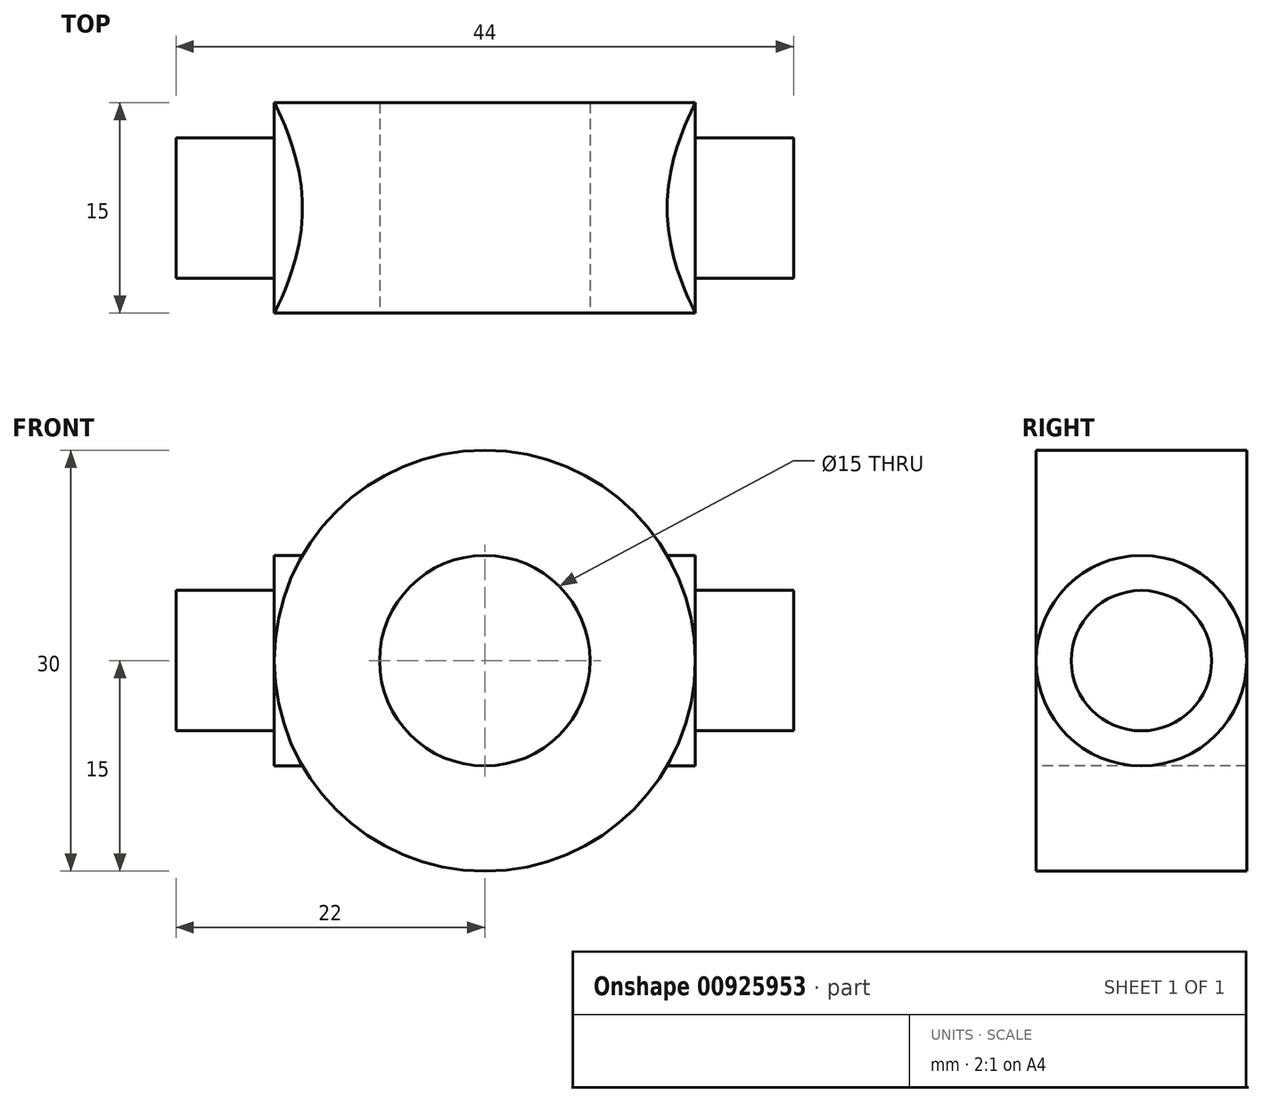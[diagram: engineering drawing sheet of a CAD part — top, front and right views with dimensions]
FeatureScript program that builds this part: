
annotation { "Feature Type Name" : "Feature", "Feature Type Description" : "" }
export const myFeature = defineFeature(function(context is Context, id is Id, definition is map)
    precondition{}
    {
        {
            var Q0;
            Q0=qCreatedBy(makeId("Front.planeOp"),FACE);
            var sketch = newSketch(context, id + "F0", { "sketchPlane" : qUnion([Q0])});
            skCircle(sketch, "E0", {"center": v(0, 0) * mm, "radius": 15 * mm});
            skSolve(sketch);
        }
        {
            var Q0;
            Q0=makeQuery(id+"F0.imprint","IMPRINT",FACE,{"disambiguationData":[TD([[makeQuery(id+"F0.imprint","IMPRINT",EDGE,{"derivedFrom":sQuery(id+"F0.wireOp",EDGE,"E0")}),1.0]])]});
            extrude(context, id + "F1", {"entities" : qUnion([Q0]), "endBound" : BoundingType.SYMMETRIC, "depth" : 15 * mm, "offsetDistance" : 25 * mm});
        }
        {
            var Q0;
            Q0=qCreatedBy(makeId("Right.planeOp"),FACE);
            var sketch = newSketch(context, id + "F2", { "sketchPlane" : qUnion([Q0])});
            skCircle(sketch, "E1", {"center": v(0, 0) * mm, "radius": 7.5 * mm});
            skSolve(sketch);
        }
        {
            var Q0;
            Q0 = qSketchRegion(id + "F2", true);
            extrude(context, id + "F3", {"entities" : qUnion([Q0]), "operationType" : NewBodyOperationType.ADD, "endBound" : BoundingType.SYMMETRIC, "depth" : 30 * mm, "offsetDistance" : 25 * mm});
        }
        {
            var Q0;
            Q0=qCreatedBy(makeId("Right.planeOp"),FACE);
            var sketch = newSketch(context, id + "F4", { "sketchPlane" : qUnion([Q0])});
            skCircle(sketch, "E2", {"center": v(0, 0) * mm, "radius": 5 * mm});
            skSolve(sketch);
        }
        {
            var Q0;
            Q0 = qSketchRegion(id + "F4", true);
            extrude(context, id + "F5", {"entities" : qUnion([Q0]), "operationType" : NewBodyOperationType.ADD, "endBound" : BoundingType.SYMMETRIC, "depth" : 44 * mm, "offsetDistance" : 25 * mm});
        }
        {
            var Q0;
            Q0=makeQuery(id+"F1.opExtrude","CAP_FACE",FACE,{"disambiguationData":[OSD([sQuery(id+"F0.wireOp",EDGE,"E0")])],"isStart":false});
            var sketch = newSketch(context, id + "F6", { "sketchPlane" : qUnion([Q0])});
            skCircle(sketch, "E3", {"center": v(0, 0) * mm, "radius": 7.5 * mm});
            skSolve(sketch);
        }
        {
            var Q0;
            Q0 = qSketchRegion(id + "F6", true);
            extrude(context, id + "F7", {"entities" : qUnion([Q0]), "operationType" : NewBodyOperationType.REMOVE, "endBound" : BoundingType.THROUGH_ALL, "oppositeDirection" : true, "depth" : 25 * mm, "offsetDistance" : 25 * mm});
        }
    });
